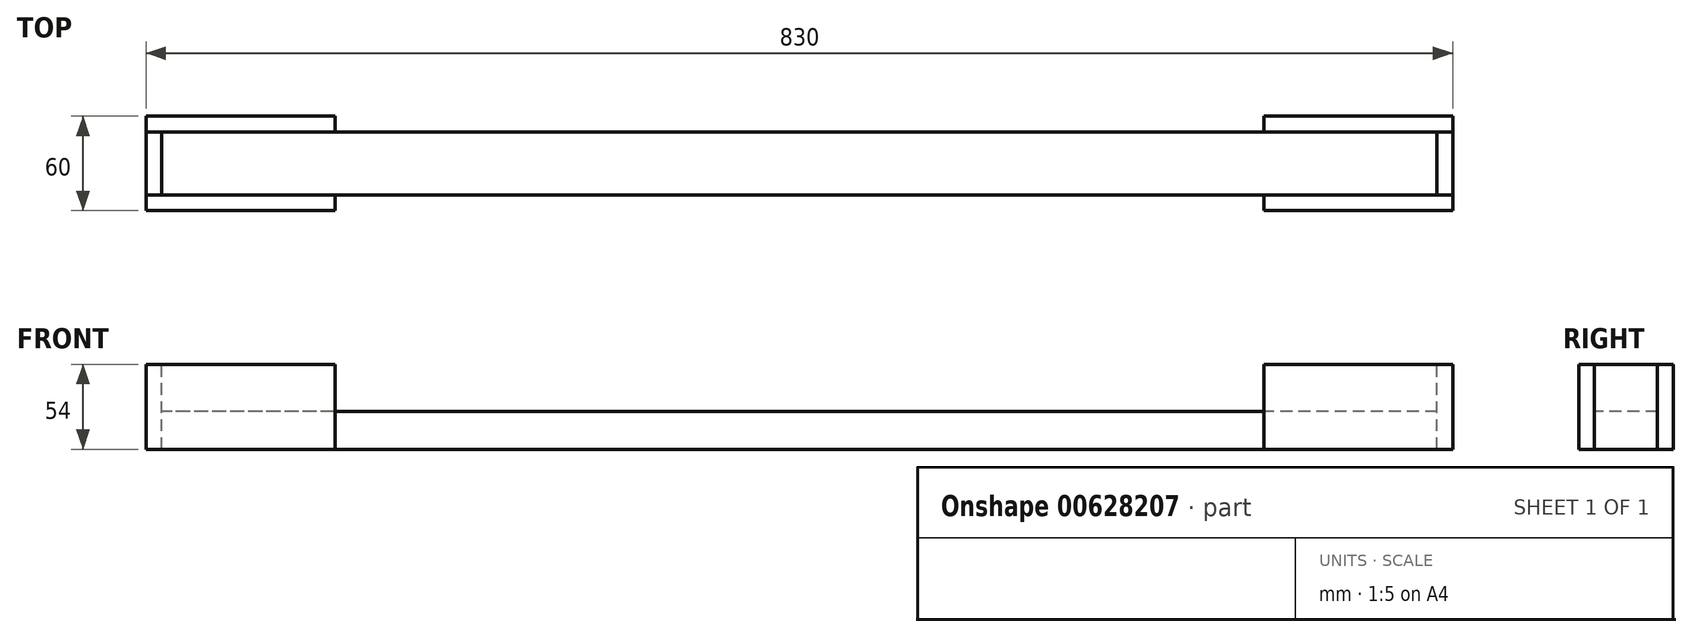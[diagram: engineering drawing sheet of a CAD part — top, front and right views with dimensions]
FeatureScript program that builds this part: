
annotation { "Feature Type Name" : "Feature", "Feature Type Description" : "" }
export const myFeature = defineFeature(function(context is Context, id is Id, definition is map)
    precondition{}
    {
        {
            var Q0;
            Q0=qCreatedBy(makeId("Right.planeOp"),FACE);
            var sketch = newSketch(context, id + "F0", { "sketchPlane" : qUnion([Q0])});
            skLineSegment(sketch, "E0.bottom", {"start": v(0, 0) * mm, "end": v(-40, 0) * mm});
            skLineSegment(sketch, "E0.top", {"start": v(0, 24) * mm, "end": v(-40, 24) * mm});
            skLineSegment(sketch, "E0.left", {"start": v(0, 0) * mm, "end": v(0, 24) * mm});
            skLineSegment(sketch, "E0.right", {"start": v(-40, 0) * mm, "end": v(-40, 24) * mm});
            skSolve(sketch);
        }
        {
            var Q0;
            Q0=makeQuery(id+"F0.imprint","IMPRINT",FACE,{"disambiguationData":[TD([[makeQuery(id+"F0.imprint","IMPRINT",EDGE,{"derivedFrom":sQuery(id+"F0.wireOp",EDGE,"E0.bottom")}),-1.0]])]});
            extrude(context, id + "F1", {"entities" : qUnion([Q0]), "depth" : 810 * mm, "offsetDistance" : 25 * mm});
        }
        {
            var Q0;
            Q0=makeQuery(id+"F1.opExtrude","CAP_FACE",FACE,{"disambiguationData":[OSD([sQuery(id+"F0.wireOp",EDGE,"E0.bottom"),sQuery(id+"F0.wireOp",EDGE,"E0.top"),sQuery(id+"F0.wireOp",EDGE,"E0.left"),sQuery(id+"F0.wireOp",EDGE,"E0.right"),sQuery(id+"F0.wireOp",EDGE,"ede54015-90a7-44e8-bfb0-7538c1eba27e.0"),sQuery(id+"F0.wireOp",EDGE,"ede54015-90a7-44e8-bfb0-7538c1eba27e.1"),sQuery(id+"F0.wireOp",EDGE,"ede54015-90a7-44e8-bfb0-7538c1eba27e.2"),sQuery(id+"F0.wireOp",EDGE,"ede54015-90a7-44e8-bfb0-7538c1eba27e.3")])],"isStart":true});
            var sketch = newSketch(context, id + "F2", { "sketchPlane" : qUnion([Q0])});
            skLineSegment(sketch, "E1.bottom", {"start": v(0, 0) * mm, "end": v(40, 0) * mm});
            skLineSegment(sketch, "E1.top", {"start": v(0, 54) * mm, "end": v(40, 54) * mm});
            skLineSegment(sketch, "E1.left", {"start": v(0, 0) * mm, "end": v(0, 54) * mm});
            skLineSegment(sketch, "E1.right", {"start": v(40, 0) * mm, "end": v(40, 54) * mm});
            skSolve(sketch);
        }
        {
            var Q0;
            Q0 = qSketchRegion(id + "F2", true);
            extrude(context, id + "F3", {"entities" : qUnion([Q0]), "depth" : 10 * mm, "offsetDistance" : 25 * mm});
        }
        {
            var Q0;
            Q0=makeQuery(id+"F3.opExtrude","SWEPT_FACE",FACE,{"disambiguationData":[OSD([sQuery(id+"F2.wireOp",EDGE,"E1.right")])]});
            var sketch = newSketch(context, id + "F4", { "sketchPlane" : qUnion([Q0])});
            skLineSegment(sketch, "E2.bottom", {"start": v(-10, 0) * mm, "end": v(110, 0) * mm});
            skLineSegment(sketch, "E2.top", {"start": v(-10, 54) * mm, "end": v(110, 54) * mm});
            skLineSegment(sketch, "E2.left", {"start": v(-10, 0) * mm, "end": v(-10, 54) * mm});
            skLineSegment(sketch, "E2.right", {"start": v(110, 0) * mm, "end": v(110, 54) * mm});
            skSolve(sketch);
        }
        {
            var Q0;
            Q0 = qSketchRegion(id + "F4", true);
            extrude(context, id + "F5", {"entities" : qUnion([Q0]), "depth" : 10 * mm, "offsetDistance" : 25 * mm});
        }
        {
            var Q0;
            Q0=makeQuery(id+"F3.opExtrude","SWEPT_FACE",FACE,{"disambiguationData":[OSD([sQuery(id+"F2.wireOp",EDGE,"E1.left")])]});
            var sketch = newSketch(context, id + "F6", { "sketchPlane" : qUnion([Q0])});
            skLineSegment(sketch, "E3.bottom", {"start": v(10, 0) * mm, "end": v(-110, 0) * mm});
            skLineSegment(sketch, "E3.top", {"start": v(10, 54) * mm, "end": v(-110, 54) * mm});
            skLineSegment(sketch, "E3.left", {"start": v(10, 0) * mm, "end": v(10, 54) * mm});
            skLineSegment(sketch, "E3.right", {"start": v(-110, 0) * mm, "end": v(-110, 54) * mm});
            skSolve(sketch);
        }
        {
            var Q0;
            Q0 = qSketchRegion(id + "F6", true);
            extrude(context, id + "F7", {"entities" : qUnion([Q0]), "depth" : 10 * mm, "offsetDistance" : 25 * mm});
        }
        {
            var Q0;
            Q0=makeQuery(id+"F1.opExtrude","SWEPT_EDGE",EDGE,{"disambiguationData":[OSD([sQuery(id+"F0.wireOp",EDGE,"E0.top"),sQuery(id+"F0.wireOp",EDGE,"E0.right")])]});
            cPoint(context, id + "F8", {"entities" : qUnion([Q0]), "parameter" : 0.5});
        }
        {
            var Q0;
            Q0=qCreatedBy(makeId("Right.planeOp"),FACE);
            var Q1;
            Q1 = qCreatedBy(id + "F8" ,VERTEX);
            cPlane(context, id + "F9", {"entities" : qUnion([Q0, Q1]), "cplaneType" : CPlaneType.PLANE_POINT, "offset" : 25 * mm, "width" : 150 * mm, "height" : 150 * mm});
        }
        {
            var Q0;
            Q0=makeQuery(id+"F5.opExtrude","SWEPT_BODY",BODY,{"disambiguationData":[OSD([sQuery(id+"F4.wireOp",EDGE,"E2.bottom"),sQuery(id+"F4.wireOp",EDGE,"E2.top"),sQuery(id+"F4.wireOp",EDGE,"E2.left"),sQuery(id+"F4.wireOp",EDGE,"E2.right")])]});
            var Q1;
            Q1=makeQuery(id+"F3.opExtrude","SWEPT_BODY",BODY,{"disambiguationData":[OSD([sQuery(id+"F2.wireOp",EDGE,"E1.bottom"),sQuery(id+"F2.wireOp",EDGE,"E1.top"),sQuery(id+"F2.wireOp",EDGE,"E1.left"),sQuery(id+"F2.wireOp",EDGE,"E1.right")])]});
            var Q2;
            Q2=makeQuery(id+"F7.opExtrude","SWEPT_BODY",BODY,{"disambiguationData":[OSD([sQuery(id+"F6.wireOp",EDGE,"E3.bottom"),sQuery(id+"F6.wireOp",EDGE,"E3.top"),sQuery(id+"F6.wireOp",EDGE,"E3.left"),sQuery(id+"F6.wireOp",EDGE,"E3.right")])]});
            var Q3;
            Q3=qCreatedBy(id+"F9.planeOp",FACE);
            mirror(context, id + "F10", {"entities" : qUnion([Q0, Q1, Q2]), "mirrorPlane" : qUnion([Q3])});
        }
    });
